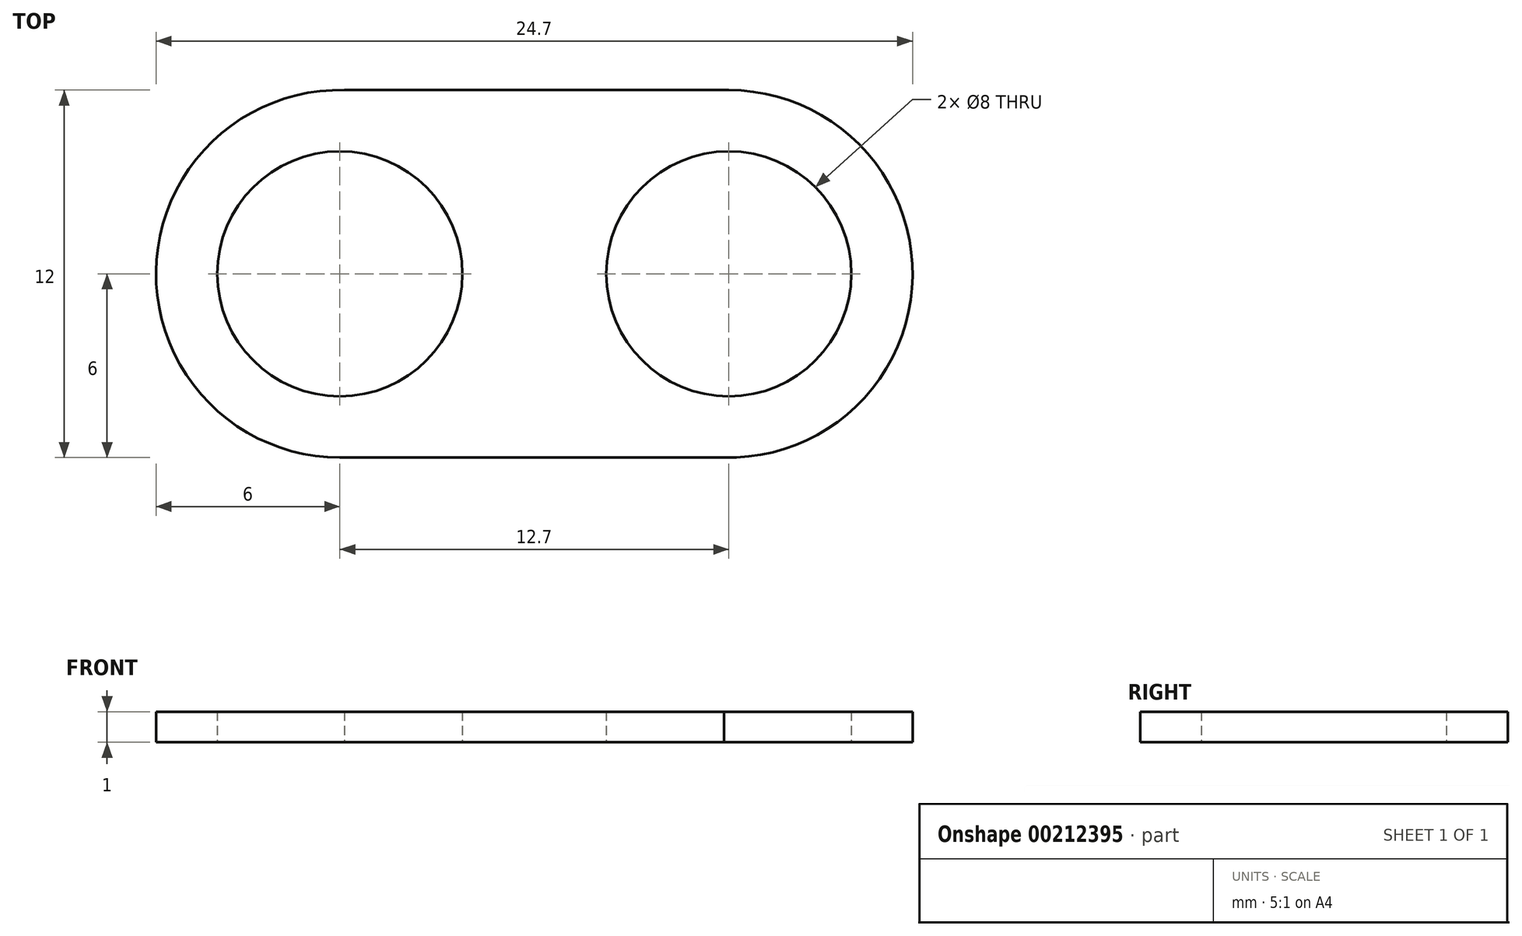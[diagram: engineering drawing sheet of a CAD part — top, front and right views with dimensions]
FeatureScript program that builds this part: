
annotation { "Feature Type Name" : "Feature", "Feature Type Description" : "" }
export const myFeature = defineFeature(function(context is Context, id is Id, definition is map)
    precondition{}
    {
        {
            var Q0;
            Q0=qCreatedBy(makeId("Top.planeOp"),FACE);
            var sketch = newSketch(context, id + "F0", { "sketchPlane" : qUnion([Q0])});
            skCircle(sketch, "E0", {"center": v(-6.35, 0) * mm, "radius": 4 * mm});
            skCircle(sketch, "E1", {"center": v(6.35, 0) * mm, "radius": 4 * mm});
            skArc(sketch, "E2", {"start": v(-6.2, 6) * mm, "mid": v(-12.35, 0.08) * mm, "end": v(-6.35, -6) * mm});
            skArc(sketch, "E3", {"start": v(6.2, -6) * mm, "mid": v(12.35, -0.08) * mm, "end": v(6.35, 6) * mm});
            skLineSegment(sketch, "E4", {"start": v(-6.2, 6) * mm, "end": v(6.35, 6) * mm});
            skLineSegment(sketch, "E5", {"start": v(6.2, -6) * mm, "end": v(-6.35, -6) * mm});
            skSolve(sketch);
        }
        {
            var Q0;
            Q0=makeQuery(id+"F0.imprint","IMPRINT",FACE,{"disambiguationData":[TD([[makeQuery(id+"F0.imprint","IMPRINT",EDGE,{"derivedFrom":sQuery(id+"F0.wireOp",EDGE,"E0")}),-1.0]])]});
            extrude(context, id + "F1", {"entities" : qUnion([Q0]), "depth" : 1 * mm});
        }
    });
